# Revit family: Скамейка стальная круглая «Сол» без спинки Арт 12987
name_source: partatom
category: Антураж
revit_build: Autodesk Revit 2018 (Build: 20180423_1000(x64)
units: mm (PartAtom-declared; Revit-internal decimal feet)

## family parameters
Всегда вертикально = Да
Источник визуального образа = Геометрия семейства
На основе рабочей плоскости = Нет
Общий = Нет
При загрузке вырезать с полостями = Нет
Точка расчета площади = Нет

## types (2) — shared parameters
URL = https://hobbyka.ru
Артикул товара = Арт. 12987
Высота = 450 мм
Группа модели = Скамейки
Изготовитель = ООО «Хоббика»
Изображение типоразмера = Скамейка стальная круглая «Сол» без спинки Арт 12987.jpg
Материал изделия = Сталь, дерево
Цвет лавки = Дерево
Цвет опоры = Сталь

## per-type parameters (varying)
| type | Версия 2,0 м | Версия 2,5 м | Длина | Описание | Ширина |
| Версия 2,0 м | Да | Нет | 2000 мм | Скамейка стальная круглая «Сол» без спинки. Версия 2,0 м | 2000 мм |
| Версия 2,5 м | Нет | Да | 2500 мм | Скамейка стальная круглая «Сол» без спинки. Версия 2,5 м | 2500 мм |
